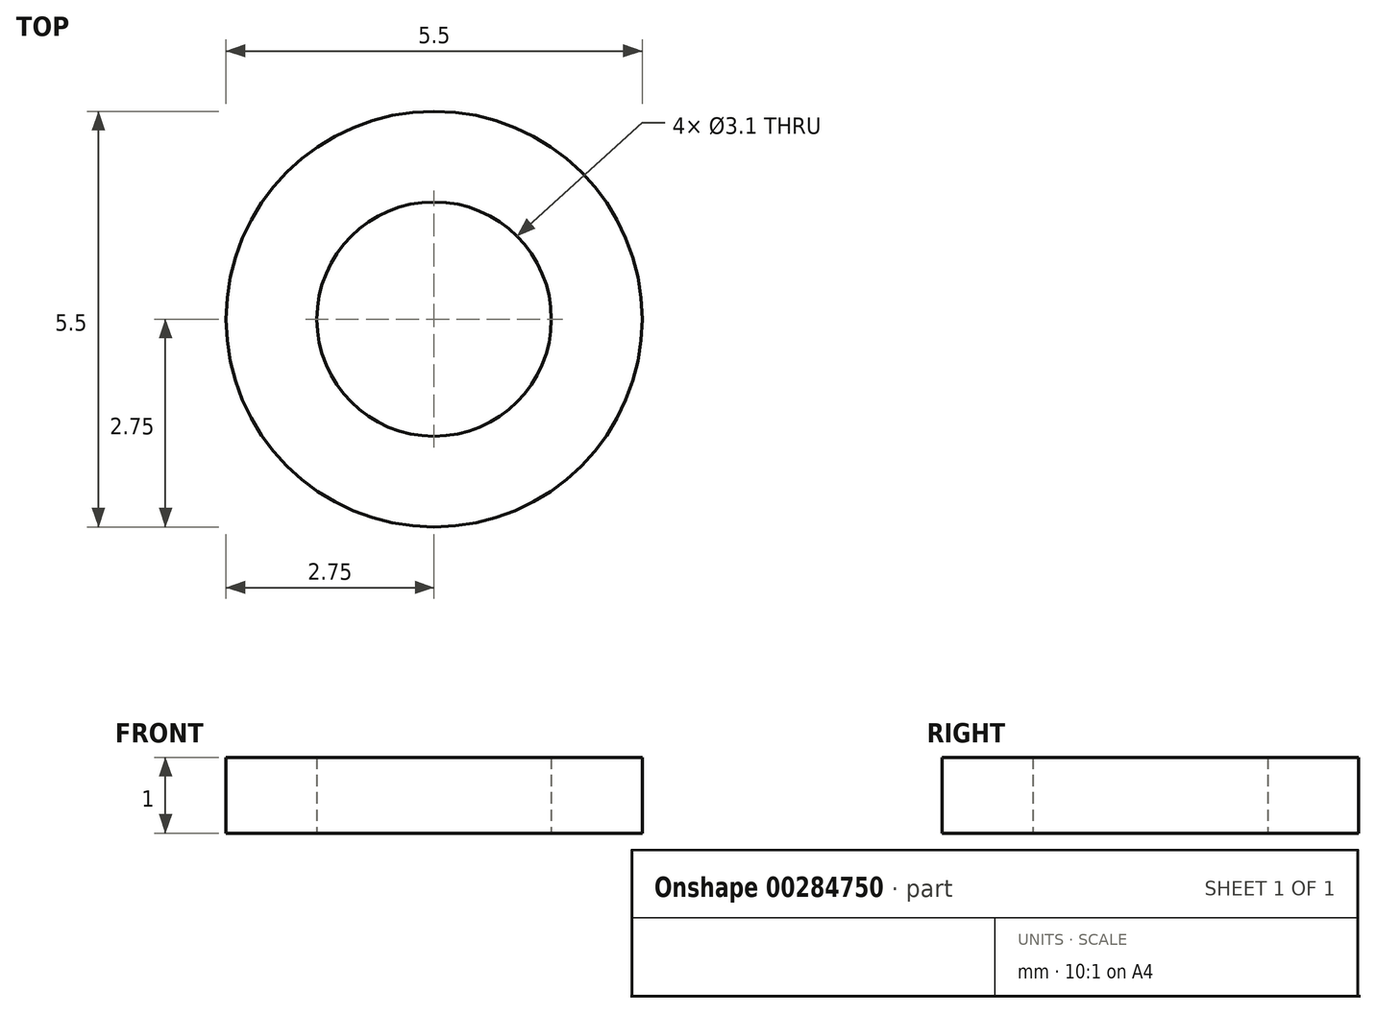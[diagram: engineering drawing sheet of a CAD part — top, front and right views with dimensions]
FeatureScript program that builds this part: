
annotation { "Feature Type Name" : "Feature", "Feature Type Description" : "" }
export const myFeature = defineFeature(function(context is Context, id is Id, definition is map)
    precondition{}
    {
        {
            var Q0;
            Q0=qCreatedBy(makeId("Top.planeOp"),FACE);
            var sketch = newSketch(context, id + "F0", { "sketchPlane" : qUnion([Q0])});
            skCircle(sketch, "E0", {"center": v(0, 0) * mm, "radius": 1.55 * mm});
            skCircle(sketch, "E1.0", {"center": v(0, 0) * mm, "radius": 2.75 * mm});
            skSolve(sketch);
        }
        {
            var Q0;
            Q0=makeQuery(id+"F0.imprint","IMPRINT",FACE,{"disambiguationData":[TD([[makeQuery(id+"F0.imprint","IMPRINT",EDGE,{"derivedFrom":sQuery(id+"F0.wireOp",EDGE,"E0")}),-1.0]])]});
            extrude(context, id + "F1", {"entities" : qUnion([Q0]), "depth" : 1 * mm});
        }
    });
